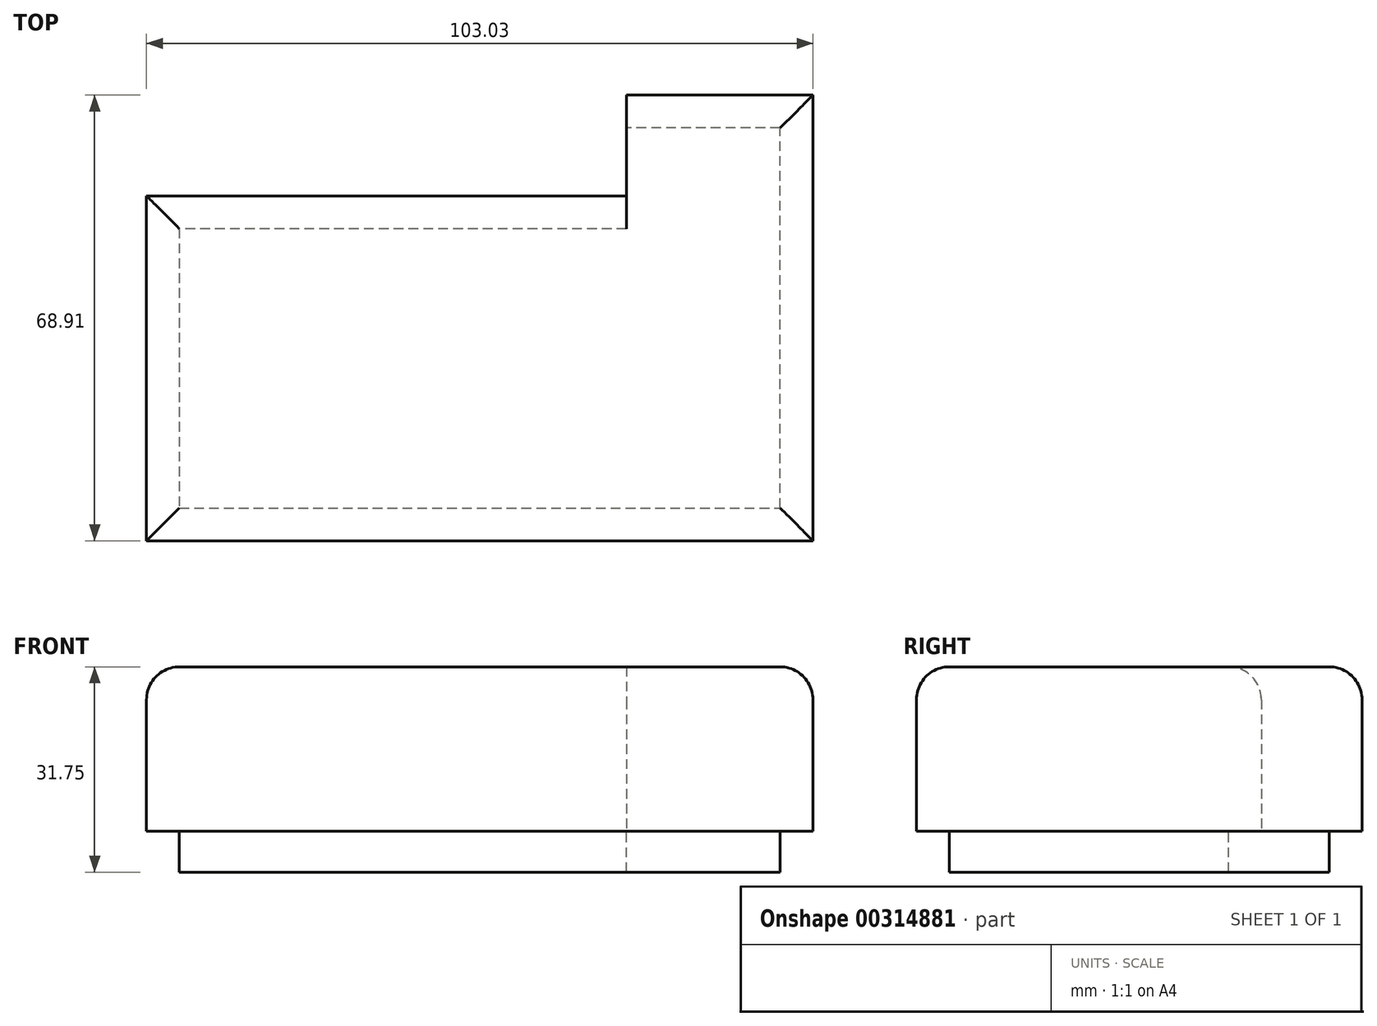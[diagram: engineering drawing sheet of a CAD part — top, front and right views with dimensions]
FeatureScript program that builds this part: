
annotation { "Feature Type Name" : "Feature", "Feature Type Description" : "" }
export const myFeature = defineFeature(function(context is Context, id is Id, definition is map)
    precondition{}
    {
        {
            var Q0;
            Q0=qCreatedBy(makeId("Top.planeOp"),FACE);
            var sketch = newSketch(context, id + "F0", { "sketchPlane" : qUnion([Q0])});
            skLineSegment(sketch, "E0.bottom", {"start": v(-33.46, 28.66) * mm, "end": v(40.75, 28.66) * mm});
            skLineSegment(sketch, "E0.top", {"start": v(-33.46, -24.68) * mm, "end": v(40.75, -24.68) * mm});
            skLineSegment(sketch, "E0.left", {"start": v(-33.46, 28.66) * mm, "end": v(-33.46, -24.68) * mm});
            skLineSegment(sketch, "E0.right", {"start": v(40.75, 28.66) * mm, "end": v(40.75, -24.68) * mm});
            skLineSegment(sketch, "E1.bottom", {"start": v(40.75, -24.68) * mm, "end": v(69.57, -24.68) * mm});
            skLineSegment(sketch, "E1.top", {"start": v(40.75, 44.23) * mm, "end": v(69.57, 44.23) * mm});
            skLineSegment(sketch, "E1.left", {"start": v(40.75, -24.68) * mm, "end": v(40.75, 44.23) * mm});
            skLineSegment(sketch, "E1.right", {"start": v(69.57, -24.68) * mm, "end": v(69.57, 44.23) * mm});
            skSolve(sketch);
        }
        {
            var Q0;
            Q0 = qSketchRegion(id + "F0", true);
            extrude(context, id + "F1", {"entities" : qUnion([Q0]), "depth" : 25.4 * mm});
        }
        {
            var Q0;
            Q0=makeQuery(id+"F1.opExtrude","CAP_EDGE",EDGE,{"disambiguationData":[OSD([sQuery(id+"F0.wireOp",EDGE,"E0.left")])],"isStart":false});
            var Q1;
            Q1=makeQuery(id+"F1.opExtrude","CAP_EDGE",EDGE,{"disambiguationData":[OSD([sQuery(id+"F0.wireOp",EDGE,"E0.bottom")])],"isStart":false});
            var Q2;
            Q2=makeQuery(id+"F1.opExtrude","CAP_EDGE",EDGE,{"disambiguationData":[OSD([sQuery(id+"F0.wireOp",EDGE,"E1.top")])],"isStart":false});
            var Q3;
            Q3=makeQuery(id+"F1.opExtrude","CAP_EDGE",EDGE,{"disambiguationData":[OSD([sQuery(id+"F0.wireOp",EDGE,"E0.top"),sQuery(id+"F0.wireOp",EDGE,"E1.bottom")])],"isStart":false});
            var Q4;
            Q4=makeQuery(id+"F1.opExtrude","CAP_EDGE",EDGE,{"disambiguationData":[OSD([sQuery(id+"F0.wireOp",EDGE,"E1.right")])],"isStart":false});
            fillet(context, id + "F2", {"entities" : qUnion([Q0, Q1, Q2, Q3, Q4]), "radius" : 5.08 * mm, "tangentPropagation" : true, "allowEdgeOverflow" : false});
        }
        {
            var Q0;
            Q0=makeQuery(id+"F1.opExtrude","CAP_FACE",FACE,{"disambiguationData":[OSD([sQuery(id+"F0.wireOp",EDGE,"E0.bottom"),sQuery(id+"F0.wireOp",EDGE,"E0.top"),sQuery(id+"F0.wireOp",EDGE,"E0.left"),sQuery(id+"F0.wireOp",EDGE,"E1.bottom"),sQuery(id+"F0.wireOp",EDGE,"E1.top"),sQuery(id+"F0.wireOp",EDGE,"E1.left"),sQuery(id+"F0.wireOp",EDGE,"E1.right")])],"isStart":false});
            var sketch = newSketch(context, id + "F3", { "sketchPlane" : qUnion([Q0])});
            skCircle(sketch, "E2", {"center": v(20.36, 0) * mm, "radius": 13.68 * mm});
            skSolve(sketch);
        }
        {
            var Q0;
            Q0 = qSketchRegion(id + "F3", true);
            var Q1;
            Q1=makeQuery(id+"F3.imprint","IMPRINT",FACE,{"disambiguationData":[TD([[makeQuery(id+"F3.imprint","IMPRINT",EDGE,{"derivedFrom":sQuery(id+"F3.wireOp",EDGE,"E2")}),-1.0]])]});
            extrude(context, id + "F4", {"entities" : qUnion([Q0, Q1]), "operationType" : NewBodyOperationType.ADD, "oppositeDirection" : true, "depth" : 31.75 * mm});
        }
    });
